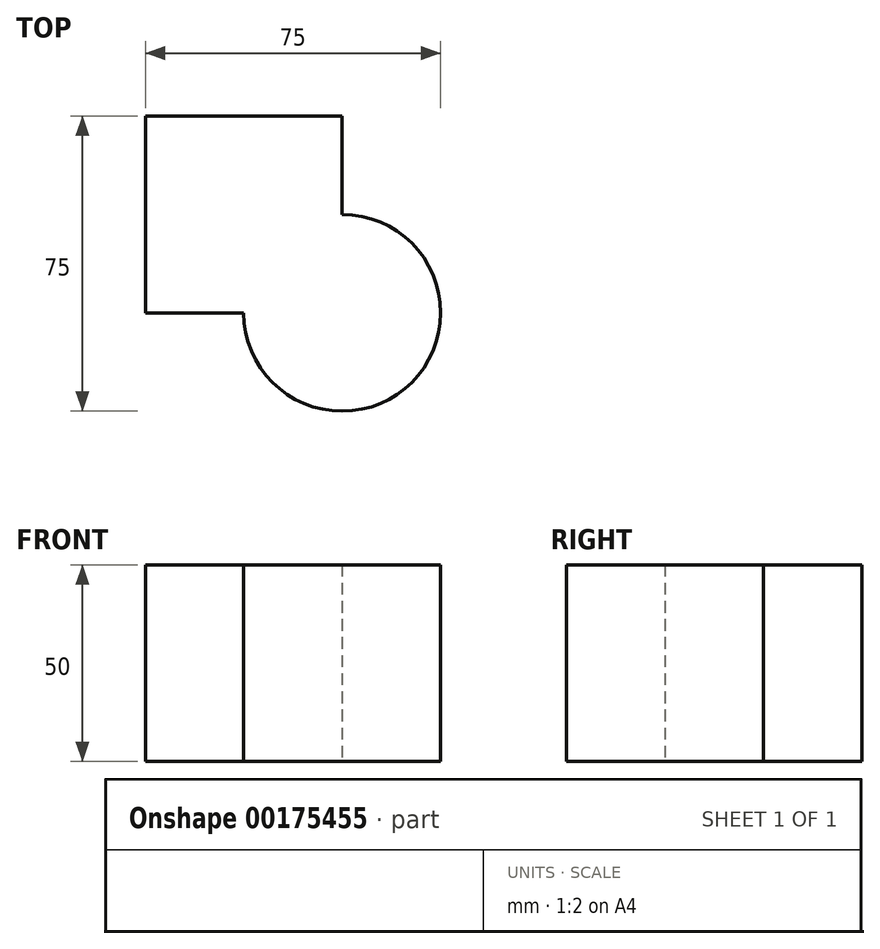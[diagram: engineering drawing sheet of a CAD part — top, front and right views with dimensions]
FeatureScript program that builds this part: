
annotation { "Feature Type Name" : "Feature", "Feature Type Description" : "" }
export const myFeature = defineFeature(function(context is Context, id is Id, definition is map)
    precondition{}
    {
        {
            var Q0;
            Q0=qCreatedBy(makeId("Top.planeOp"),FACE);
            var sketch = newSketch(context, id + "F0", { "sketchPlane" : qUnion([Q0])});
            skLineSegment(sketch, "E0.bottom", {"start": v(-19.8, 28.1) * mm, "end": v(30.2, 28.1) * mm});
            skLineSegment(sketch, "E0.top", {"start": v(-19.8, -21.9) * mm, "end": v(30.2, -21.9) * mm});
            skLineSegment(sketch, "E0.left", {"start": v(-19.8, 28.1) * mm, "end": v(-19.8, -21.9) * mm});
            skLineSegment(sketch, "E0.right", {"start": v(30.2, 28.1) * mm, "end": v(30.2, -21.9) * mm});
            skCircle(sketch, "E1", {"center": v(30.2, -21.9) * mm, "radius": 25 * mm});
            skSolve(sketch);
        }
        {
            var Q0;
            Q0 = qSketchRegion(id + "F0", true);
            extrude(context, id + "F1", {"entities" : qUnion([Q0]), "depth" : 50 * mm});
        }
    });
